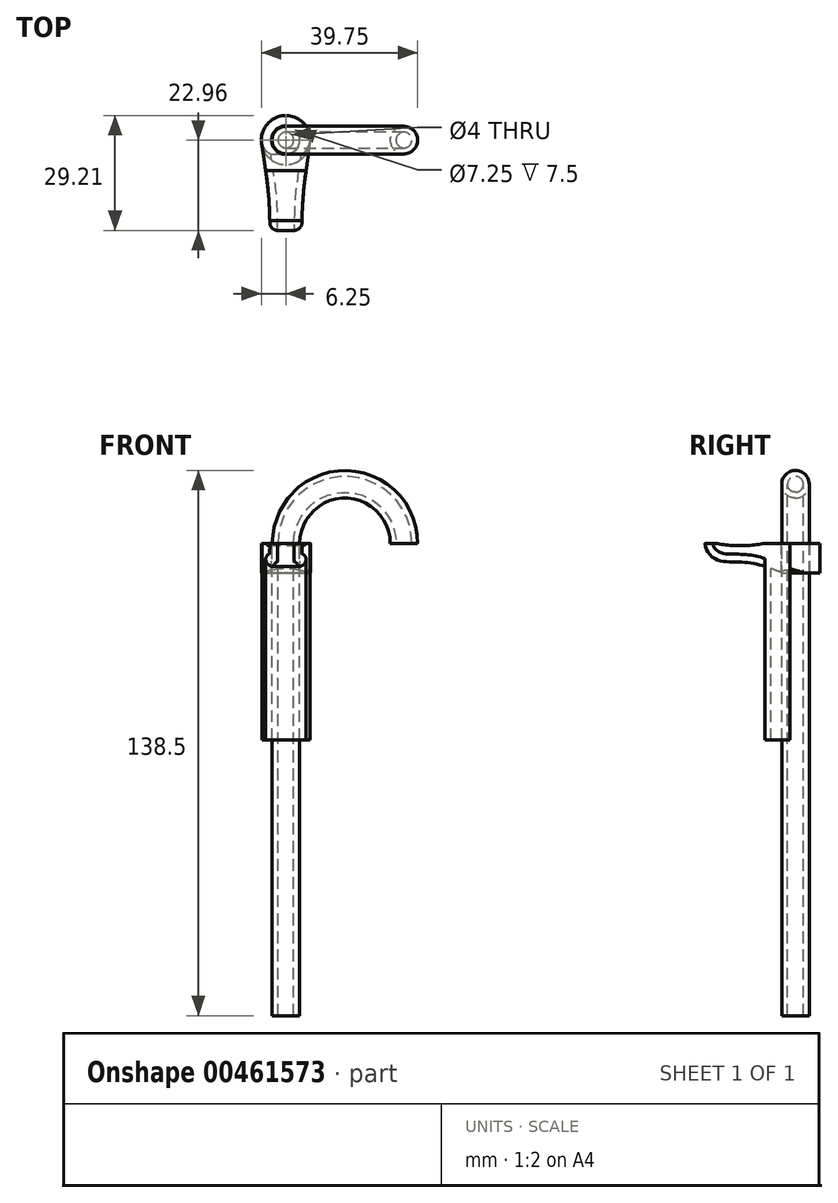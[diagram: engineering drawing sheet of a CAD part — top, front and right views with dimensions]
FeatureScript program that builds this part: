
annotation { "Feature Type Name" : "Feature", "Feature Type Description" : "" }
export const myFeature = defineFeature(function(context is Context, id is Id, definition is map)
    precondition{}
    {
        {
            var Q0;
            Q0=qCreatedBy(makeId("Front.planeOp"),FACE);
            var sketch = newSketch(context, id + "F0", { "sketchPlane" : qUnion([Q0])});
            skLineSegment(sketch, "E0", {"start": v(0, 0) * mm, "end": v(0, 120) * mm});
            skArc(sketch, "E1", {"start": v(0, 120) * mm, "mid": v(15, 135) * mm, "end": v(30, 120) * mm});
            skSolve(sketch);
        }
        {
            var Q0;
            Q0=qCreatedBy(makeId("Top.planeOp"),FACE);
            var sketch = newSketch(context, id + "F1", { "sketchPlane" : qUnion([Q0])});
            skCircle(sketch, "E2", {"center": v(0, 0) * mm, "radius": 3.5 * mm});
            skCircle(sketch, "E3", {"center": v(0, 0) * mm, "radius": 2 * mm});
            skSolve(sketch);
        }
        {
            var Q0;
            Q0=makeQuery(id+"F1.imprint","IMPRINT",FACE,{"disambiguationData":[TD([[makeQuery(id+"F1.imprint","IMPRINT",EDGE,{"derivedFrom":sQuery(id+"F1.wireOp",EDGE,"E2")}),1.0]])]});
            var Q1;
            Q1=sQuery(id+"F0.wireOp",EDGE,"E0");
            var Q2;
            Q2=sQuery(id+"F0.wireOp",EDGE,"E1");
            sweep(context, id + "F2", {"profiles" : qUnion([Q0]), "path" : qUnion([Q1, Q2])});
        }
        {
            var Q0;
            Q0=makeQuery(id+"F2.opSweep","CAP_FACE",FACE,{"disambiguationData":[OSD([sQuery(id+"F0.wireOp",VERTEX,"E1.end"),sQuery(id+"F1.wireOp",EDGE,"E2"),sQuery(id+"F1.wireOp",EDGE,"E3")])],"isStart":false});
            var sketch = newSketch(context, id + "F3", { "sketchPlane" : qUnion([Q0])});
            skCircle(sketch, "E4", {"center": v(0, 0) * mm, "radius": 6.25 * mm});
            skCircle(sketch, "E5", {"center": v(0, 0) * mm, "radius": 3.62 * mm});
            skSolve(sketch);
        }
        {
            var Q0;
            Q0=makeQuery(id+"F3.imprint","IMPRINT",FACE,{"disambiguationData":[TD([[makeQuery(id+"F3.imprint","IMPRINT",EDGE,{"derivedFrom":sQuery(id+"F3.wireOp",EDGE,"E4")}),1.0]])]});
            extrude(context, id + "F4", {"entities" : qUnion([Q0]), "depth" : 7.5 * mm});
        }
        {
            var Q0;
            Q0=makeQuery(id+"F4.opExtrude","CAP_FACE",FACE,{"disambiguationData":[OSD([sQuery(id+"F3.wireOp",EDGE,"E4"),sQuery(id+"F3.wireOp",EDGE,"E5")])],"isStart":true});
            var sketch = newSketch(context, id + "F5", { "sketchPlane" : qUnion([Q0])});
            skLineSegment(sketch, "E6", {"start": v(0, 0) * mm, "end": v(0, -32.2) * mm, "construction": true});
            skLineSegment(sketch, "E7", {"start": v(0, -22.96) * mm, "end": v(-4, -22.96) * mm});
            skFitSpline(sketch, "E8", {"points": [v(-6.22, -0.56) * mm, v(-4.54, -12.58) * mm, v(-4, -22.96) * mm], "startDerivative": vector(1.01, -5.82) * mm, "endDerivative": vector(1, -24.36) * mm});
            skLineSegment(sketch, "E9.MirrorCS", {"start": v(0, -22.96) * mm, "end": v(4, -22.96) * mm});
            skFitSpline(sketch, "E10.MirrorCS", {"points": [v(6.22, -0.56) * mm, v(4.54, -12.58) * mm, v(4, -22.96) * mm], "startDerivative": vector(-1.01, -5.82) * mm, "endDerivative": vector(-1, -24.36) * mm});
            skSolve(sketch);
        }
        {
            var Q0;
            {var subQ2=sQuery(id+"F5.wireOp",EDGE,"E7");Q0=makeQuery(id+"F5.imprint","IMPRINT",FACE,{"disambiguationData":[TD([[makeQuery(id+"F5.imprint","IMPRINT",EDGE,{"derivedFrom":subQ2}),-1.0]])]});}
            var Q1;
            Q1=makeQuery(id+"F4.opExtrude","CAP_FACE",FACE,{"disambiguationData":[OSD([sQuery(id+"F3.wireOp",EDGE,"E4"),sQuery(id+"F3.wireOp",EDGE,"E5")])],"isStart":false});
            extrude(context, id + "F6", {"entities" : qUnion([Q0]), "operationType" : NewBodyOperationType.ADD, "endBound" : BoundingType.UP_TO_SURFACE, "oppositeDirection" : true, "endBoundEntityFace" : qUnion([Q1]), "depth" : 25 * mm});
        }
        {
            var Q0;
            Q0=qCreatedBy(makeId("Right.planeOp"),FACE);
            var sketch = newSketch(context, id + "F7", { "sketchPlane" : qUnion([Q0])});
            skLineSegment(sketch, "E11", {"start": v(-3.5, 0) * mm, "end": v(-3.5, 120) * mm, "construction": true});
            skFitSpline(sketch, "E12.0", {"points": [v(-0.56, 112.5) * mm, v(-1.57, 112.5) * mm, v(-14.18, 112.5) * mm, v(-19.05, 112.5) * mm, v(-22.96, 112.5) * mm], "construction": true});
            skLineSegment(sketch, "E13.0", {"start": v(-22.96, 112.5) * mm, "end": v(-22.96, 120) * mm, "construction": true});
            skFitSpline(sketch, "E14", {"points": [v(-3.5, 112.5) * mm, v(-12.17, 115.12) * mm, v(-20.08, 115.92) * mm, v(-22.96, 120) * mm], "startDerivative": vector(-21.25, 9.26) * mm, "endDerivative": vector(-0.1, 18.45) * mm});
            skFitSpline(sketch, "E15.0", {"points": [v(-0.56, 120) * mm, v(-1.57, 120) * mm, v(-14.18, 120) * mm, v(-19.05, 120) * mm, v(-22.96, 120) * mm], "construction": true});
            skArc(sketch, "E16", {"start": v(-20.42, 120) * mm, "mid": v(-14.05, 119.43) * mm, "end": v(-7.7, 120) * mm});
            skLineSegment(sketch, "E17", {"start": v(-7.7, 120) * mm, "end": v(-20.42, 120) * mm});
            skLineSegment(sketch, "E18", {"start": v(-22.96, 120) * mm, "end": v(-22.96, 112.5) * mm});
            skLineSegment(sketch, "E19", {"start": v(-3.5, 112.5) * mm, "end": v(-22.96, 112.5) * mm});
            skSolve(sketch);
        }
        {
            var Q0;
            Q0 = qSketchRegion(id + "F7", true);
            extrude(context, id + "F8", {"entities" : qUnion([Q0]), "operationType" : NewBodyOperationType.REMOVE, "endBound" : BoundingType.SYMMETRIC, "oppositeDirection" : true, "depth" : 25 * mm});
        }
        {
            var Q0;
            Q0=makeQuery(id+"F8.boolean.opBoolean","INTERSECT",EDGE,{"derivedFrom":[makeQuery(id+"F6.opExtrude","SWEPT_FACE",FACE,{"disambiguationData":[OSD([sQuery(id+"F5.wireOp",EDGE,"E8")])]}),makeQuery(id+"F8.opExtrude","SWEPT_FACE",FACE,{"disambiguationData":[OSD([sQuery(id+"F7.wireOp",EDGE,"E14")])]})]});
            var Q1;
            Q1=makeQuery(id+"F8.boolean.opBoolean","INTERSECT",EDGE,{"derivedFrom":[makeQuery(id+"F6.opExtrude","SWEPT_FACE",FACE,{"disambiguationData":[OSD([sQuery(id+"F5.wireOp",EDGE,"E10.MirrorCS")])]}),makeQuery(id+"F8.opExtrude","SWEPT_FACE",FACE,{"disambiguationData":[OSD([sQuery(id+"F7.wireOp",EDGE,"E14")])]})]});
            fillet(context, id + "F9", {"entities" : qUnion([Q0, Q1]), "radius" : 2 * mm, "tangentPropagation" : true, "allowEdgeOverflow" : false});
        }
        {
            var Q0;
            {var subQ0=sQuery(id+"F5.wireOp",EDGE,"E10.MirrorCS");var subQ1=sQuery(id+"F5.wireOp",EDGE,"E8");var subQ2=sQuery(id+"F3.wireOp",EDGE,"E5");var subQ3=sQuery(id+"F3.wireOp",EDGE,"E4");Q0=makeQuery(id+"F8.boolean.opBoolean","SPLIT",FACE,{"disambiguationData":[TD([makeQuery(id+"F4.opExtrude","SWEPT_FACE",FACE,{"disambiguationData":[OSD([subQ3])]})])],"derivedFrom":makeQuery(id+"F6.boolean.opBoolean","MERGE",FACE,{"derivedFrom":[makeQuery(id+"F4.opExtrude","CAP_FACE",FACE,{"disambiguationData":[OSD([subQ3,subQ2])],"isStart":true}),makeQuery(id+"F6.opExtrude","CAP_FACE",FACE,{"disambiguationData":[OSD([subQ3,sQuery(id+"F5.wireOp",EDGE,"E7"),subQ1,sQuery(id+"F5.wireOp",EDGE,"E9.MirrorCS"),subQ0])],"isStart":true})]})});}
            var sketch = newSketch(context, id + "F10", { "sketchPlane" : qUnion([Q0])});
            skCircle(sketch, "E20", {"center": v(0, 0) * mm, "radius": 6.25 * mm});
            skCircle(sketch, "E21.0", {"center": v(0, 0) * mm, "radius": 3.62 * mm});
            skSolve(sketch);
        }
        {
            var Q0;
            {var subQ0=sQuery(id+"F10.wireOp",EDGE,"E20");Q0=makeQuery(id+"F10.imprint","IMPRINT",FACE,{"disambiguationData":[TD([[makeQuery(id+"F10.imprint","IMPRINT",EDGE,{"disambiguationData":[OD(0.0)],"derivedFrom":subQ0}),-1.0]])]});}
            extrude(context, id + "F11", {"entities" : qUnion([Q0]), "operationType" : NewBodyOperationType.ADD, "oppositeDirection" : true, "depth" : 50 * mm});
        }
    });
